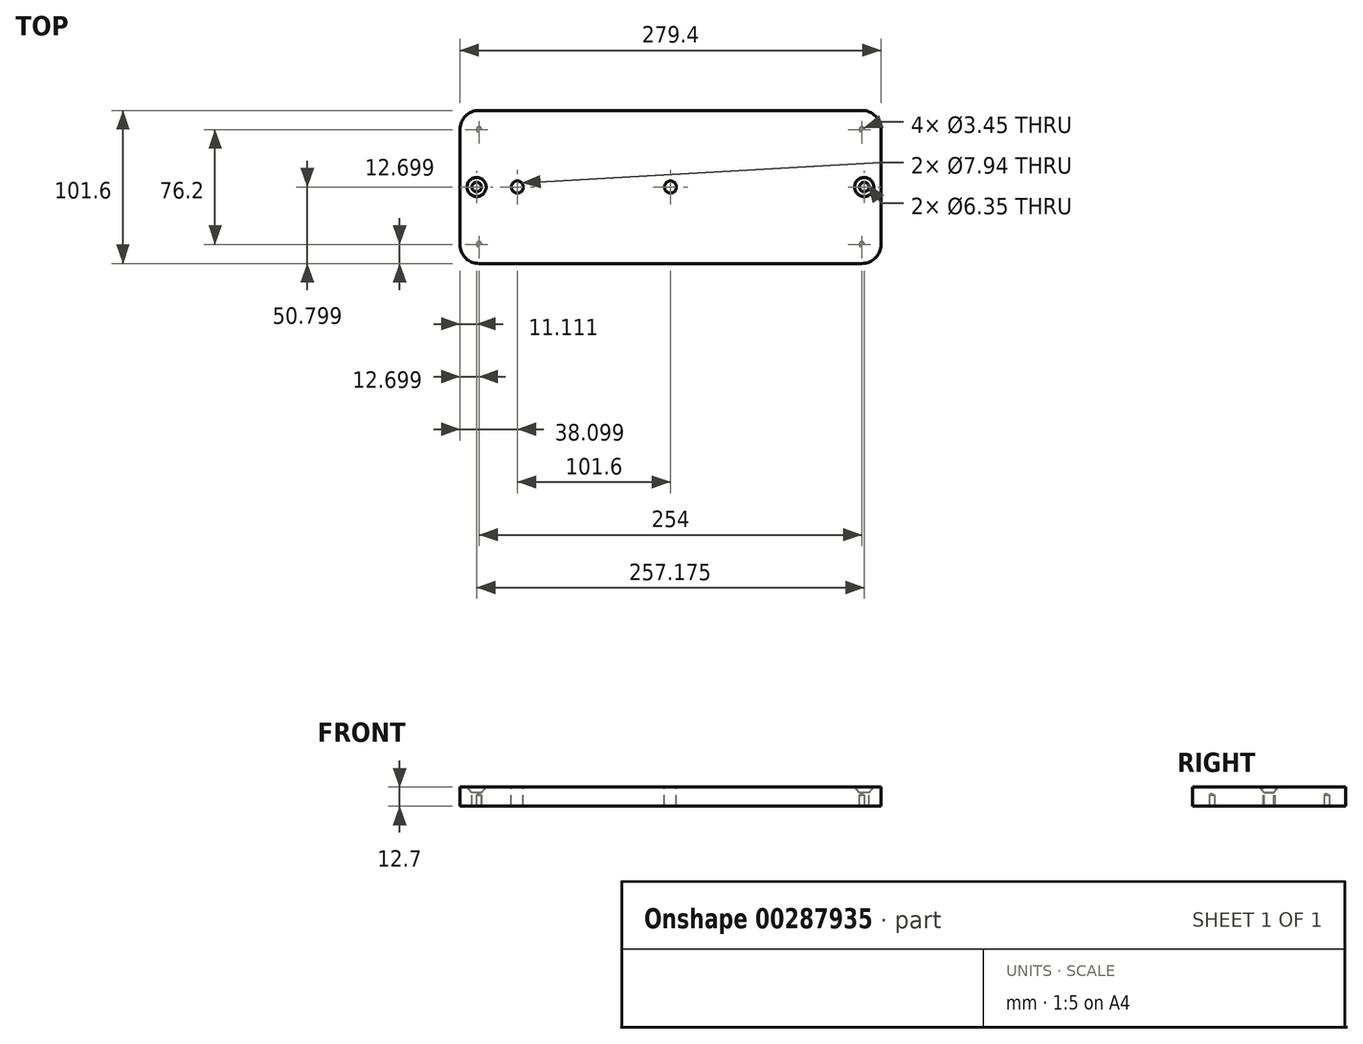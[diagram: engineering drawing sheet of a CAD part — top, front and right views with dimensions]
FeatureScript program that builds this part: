
annotation { "Feature Type Name" : "Feature", "Feature Type Description" : "" }
export const myFeature = defineFeature(function(context is Context, id is Id, definition is map)
    precondition{}
    {
        {
            var Q0;
            Q0=qCreatedBy(makeId("Top.planeOp"),FACE);
            var sketch = newSketch(context, id + "F0", { "sketchPlane" : qUnion([Q0])});
            skLineSegment(sketch, "E0.bottom", {"start": v(-190.34, 91.2) * mm, "end": v(89.06, 91.2) * mm});
            skLineSegment(sketch, "E0.top", {"start": v(-190.34, -10.4) * mm, "end": v(89.06, -10.4) * mm});
            skLineSegment(sketch, "E0.left", {"start": v(-190.34, 91.2) * mm, "end": v(-190.34, -10.4) * mm});
            skLineSegment(sketch, "E0.right", {"start": v(89.06, 91.2) * mm, "end": v(89.06, -10.4) * mm});
            skSolve(sketch);
        }
        {
            var Q0;
            Q0=makeQuery(id+"F0.imprint","IMPRINT",FACE,{"disambiguationData":[TD([[makeQuery(id+"F0.imprint","IMPRINT",EDGE,{"derivedFrom":sQuery(id+"F0.wireOp",EDGE,"E0.bottom")}),-1.0]])]});
            extrude(context, id + "F1", {"entities" : qUnion([Q0]), "depth" : 12.7 * mm, "offsetDistance" : 25.4 * mm});
        }
        {
            var Q0;
            Q0=makeQuery(id+"F1.opExtrude","CAP_FACE",FACE,{"disambiguationData":[OSD([sQuery(id+"F0.wireOp",EDGE,"E0.bottom"),sQuery(id+"F0.wireOp",EDGE,"E0.top"),sQuery(id+"F0.wireOp",EDGE,"E0.left"),sQuery(id+"F0.wireOp",EDGE,"E0.right")])],"isStart":false});
            var sketch = newSketch(context, id + "F2", { "sketchPlane" : qUnion([Q0])});
            skPoint(sketch, "E1", {"position": v(-179.23, 40.4) * mm});
            skPoint(sketch, "E2", {"position": v(-152.24, 40.4) * mm});
            skPoint(sketch, "E3", {"position": v(-50.64, 40.4) * mm});
            skPoint(sketch, "E4", {"position": v(77.95, 40.4) * mm});
            skLineSegment(sketch, "E5", {"start": v(-203.05, 40.4) * mm, "end": v(99.7, 40.4) * mm, "construction": true});
            skSolve(sketch);
        }
        {
            var Q0;
            Q0=makeQuery(id+"F1.opExtrude","SWEPT_EDGE",EDGE,{"disambiguationData":[OSD([sQuery(id+"F0.wireOp",EDGE,"E0.bottom"),sQuery(id+"F0.wireOp",EDGE,"E0.right")])]});
            var Q1;
            Q1=makeQuery(id+"F1.opExtrude","SWEPT_EDGE",EDGE,{"disambiguationData":[OSD([sQuery(id+"F0.wireOp",EDGE,"E0.top"),sQuery(id+"F0.wireOp",EDGE,"E0.right")])]});
            var Q2;
            Q2=makeQuery(id+"F1.opExtrude","SWEPT_EDGE",EDGE,{"disambiguationData":[OSD([sQuery(id+"F0.wireOp",EDGE,"E0.bottom"),sQuery(id+"F0.wireOp",EDGE,"E0.left")])]});
            var Q3;
            Q3=makeQuery(id+"F1.opExtrude","SWEPT_EDGE",EDGE,{"disambiguationData":[OSD([sQuery(id+"F0.wireOp",EDGE,"E0.top"),sQuery(id+"F0.wireOp",EDGE,"E0.left")])]});
            fillet(context, id + "F3", {"entities" : qUnion([Q0, Q1, Q2, Q3]), "radius" : 12.7 * mm, "tangentPropagation" : true, "allowEdgeOverflow" : false});
        }
        {
            var Q0;
            Q0=makeQuery(id+"F1.opExtrude","CAP_FACE",FACE,{"disambiguationData":[OSD([sQuery(id+"F0.wireOp",EDGE,"E0.bottom"),sQuery(id+"F0.wireOp",EDGE,"E0.top"),sQuery(id+"F0.wireOp",EDGE,"E0.left"),sQuery(id+"F0.wireOp",EDGE,"E0.right")])],"isStart":true});
            var sketch = newSketch(context, id + "F4", { "sketchPlane" : qUnion([Q0])});
            skPoint(sketch, "E6", {"position": v(76.36, -2.3) * mm});
            skPoint(sketch, "E7", {"position": v(76.36, -78.5) * mm});
            skPoint(sketch, "E8", {"position": v(-177.64, -78.5) * mm});
            skPoint(sketch, "E9", {"position": v(-177.64, -2.3) * mm});
            skSolve(sketch);
        }
        {
            var Q0;
            Q0=sQuery(id+"F4.wireOp",VERTEX,"E9");
            var Q1;
            Q1=sQuery(id+"F4.wireOp",VERTEX,"E8");
            var Q2;
            Q2=sQuery(id+"F4.wireOp",VERTEX,"E6");
            var Q3;
            Q3=sQuery(id+"F4.wireOp",VERTEX,"E7");
            var Q4;
            Q4=makeQuery(id+"F1.opExtrude","SWEPT_BODY",BODY,{"disambiguationData":[OSD([sQuery(id+"F0.wireOp",EDGE,"E0.bottom"),sQuery(id+"F0.wireOp",EDGE,"E0.top"),sQuery(id+"F0.wireOp",EDGE,"E0.left"),sQuery(id+"F0.wireOp",EDGE,"E0.right")])]});
            hole(context, id + "F5", {"style" : HoleStyle.SIMPLE, "endStyle" : HoleEndStyle.BLIND, "standardTappedOrClearance" : lookupTablePath({ "standard" : "ANSI", "engagement" : "75%", "pitch" : "32 tpi", "size" : "#8", "type" : "Tapped" }), "standardBlindInLast" : lookupTablePath({ "standard" : "ANSI", "engagement" : "75%", "pitch" : "32 tpi", "size" : "#8", "type" : "Tapped" }), "holeDiameter" : 3.45 * mm, "majorDiameter" : 4.17 * mm, "showTappedDepth" : true, "holeDepth" : 7.3 * mm, "isTappedThrough" : true, "tappedDepth" : 4.92 * mm, "tapClearance" : 3, "locations" : qUnion([Q0, Q1, Q2, Q3]), "scope" : qUnion([Q4])});
        }
        {
            var Q0;
            Q0=sQuery(id+"F2.wireOp",VERTEX,"E2");
            var Q1;
            Q1=sQuery(id+"F2.wireOp",VERTEX,"E3");
            var Q2;
            Q2=makeQuery(id+"F1.opExtrude","SWEPT_BODY",BODY,{"disambiguationData":[OSD([sQuery(id+"F0.wireOp",EDGE,"E0.bottom"),sQuery(id+"F0.wireOp",EDGE,"E0.top"),sQuery(id+"F0.wireOp",EDGE,"E0.left"),sQuery(id+"F0.wireOp",EDGE,"E0.right")])]});
            hole(context, id + "F6", {"style" : HoleStyle.SIMPLE, "endStyle" : HoleEndStyle.THROUGH, "holeDiameter" : 7.94 * mm, "majorDiameter" : 4.17 * mm, "isTappedThrough" : true, "tappedDepth" : 4.92 * mm, "tapClearance" : 3, "locations" : qUnion([Q0, Q1]), "scope" : qUnion([Q2])});
        }
        {
            var Q0;
            Q0=sQuery(id+"F2.wireOp",VERTEX,"E1");
            var Q1;
            Q1=sQuery(id+"F2.wireOp",VERTEX,"E4");
            var Q2;
            Q2=makeQuery(id+"F1.opExtrude","SWEPT_BODY",BODY,{"disambiguationData":[OSD([sQuery(id+"F0.wireOp",EDGE,"E0.bottom"),sQuery(id+"F0.wireOp",EDGE,"E0.top"),sQuery(id+"F0.wireOp",EDGE,"E0.left"),sQuery(id+"F0.wireOp",EDGE,"E0.right")])]});
            hole(context, id + "F7", {"style" : HoleStyle.C_SINK, "endStyle" : HoleEndStyle.BLIND, "holeDiameter" : 6.35 * mm, "cSinkDiameter" : 12.7 * mm, "cSinkAngle" : 82 * degree, "majorDiameter" : 6.35 * mm, "holeDepth" : 25.4 * mm, "isTappedThrough" : true, "tappedDepth" : 4.93 * mm, "tapClearance" : 3, "locations" : qUnion([Q0, Q1]), "scope" : qUnion([Q2])});
        }
    });
